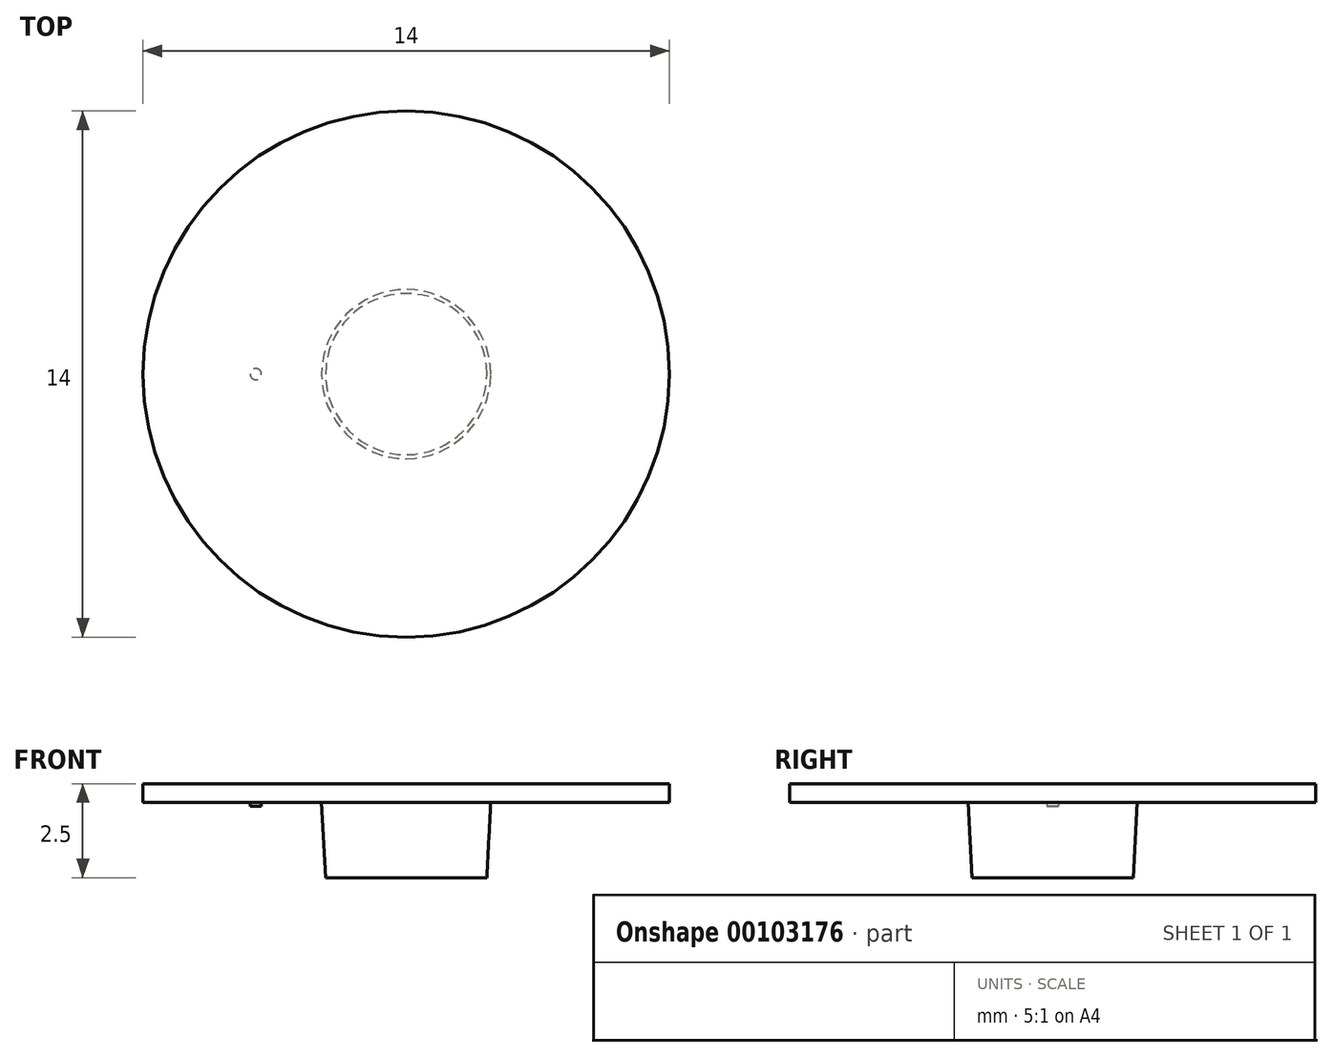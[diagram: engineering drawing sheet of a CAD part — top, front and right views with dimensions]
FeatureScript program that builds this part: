
annotation { "Feature Type Name" : "Feature", "Feature Type Description" : "" }
export const myFeature = defineFeature(function(context is Context, id is Id, definition is map)
    precondition{}
    {
        {
            var Q0;
            Q0=qCreatedBy(makeId("Top.planeOp"),FACE);
            var sketch = newSketch(context, id + "F0", { "sketchPlane" : qUnion([Q0])});
            skCircle(sketch, "E0", {"center": v(0, 0) * mm, "radius": 2.25 * mm});
            skSolve(sketch);
        }
        {
            var Q0;
            Q0 = qSketchRegion(id + "F0", true);
            extrude(context, id + "F1", {"entities" : qUnion([Q0]), "oppositeDirection" : true, "depth" : 2 * mm, "hasDraft" : true, "draftAngle" : 3 * degree, "draftPullDirection" : true});
        }
        {
            var Q0;
            Q0=qCreatedBy(makeId("Top.planeOp"),FACE);
            var sketch = newSketch(context, id + "F2", { "sketchPlane" : qUnion([Q0])});
            skCircle(sketch, "E1", {"center": v(0, 0) * mm, "radius": 7 * mm});
            skSolve(sketch);
        }
        {
            var Q0;
            Q0 = qSketchRegion(id + "F2", true);
            extrude(context, id + "F3", {"entities" : qUnion([Q0]), "operationType" : NewBodyOperationType.ADD, "depth" : .5 * mm});
        }
        {
            var Q0;
            Q0=makeQuery(id+"F1.opExtrude","SWEPT_BODY",BODY,{"disambiguationData":[OSD([sQuery(id+"F0.wireOp",EDGE,"E0")])]});
            transform(context, id + "F4", {"entities" : qUnion([Q0]), "transformType" : TransformType.TRANSLATION_3D, "dx" : 0 * mm, "dy" : 0 * mm, "dz" : .1 * mm, "makeCopy" : false});
        }
        {
            var Q0;
            Q0=qCreatedBy(makeId("Top.planeOp"),FACE);
            var sketch = newSketch(context, id + "F5", { "sketchPlane" : qUnion([Q0])});
            skCircle(sketch, "E2", {"center": v(-4, 0) * mm, "radius": 0.15 * mm});
            skSolve(sketch);
        }
        {
            var Q0;
            Q0 = qSketchRegion(id + "F5", true);
            extrude(context, id + "F6", {"entities" : qUnion([Q0]), "operationType" : NewBodyOperationType.ADD, "depth" : .1 * mm});
        }
    });
